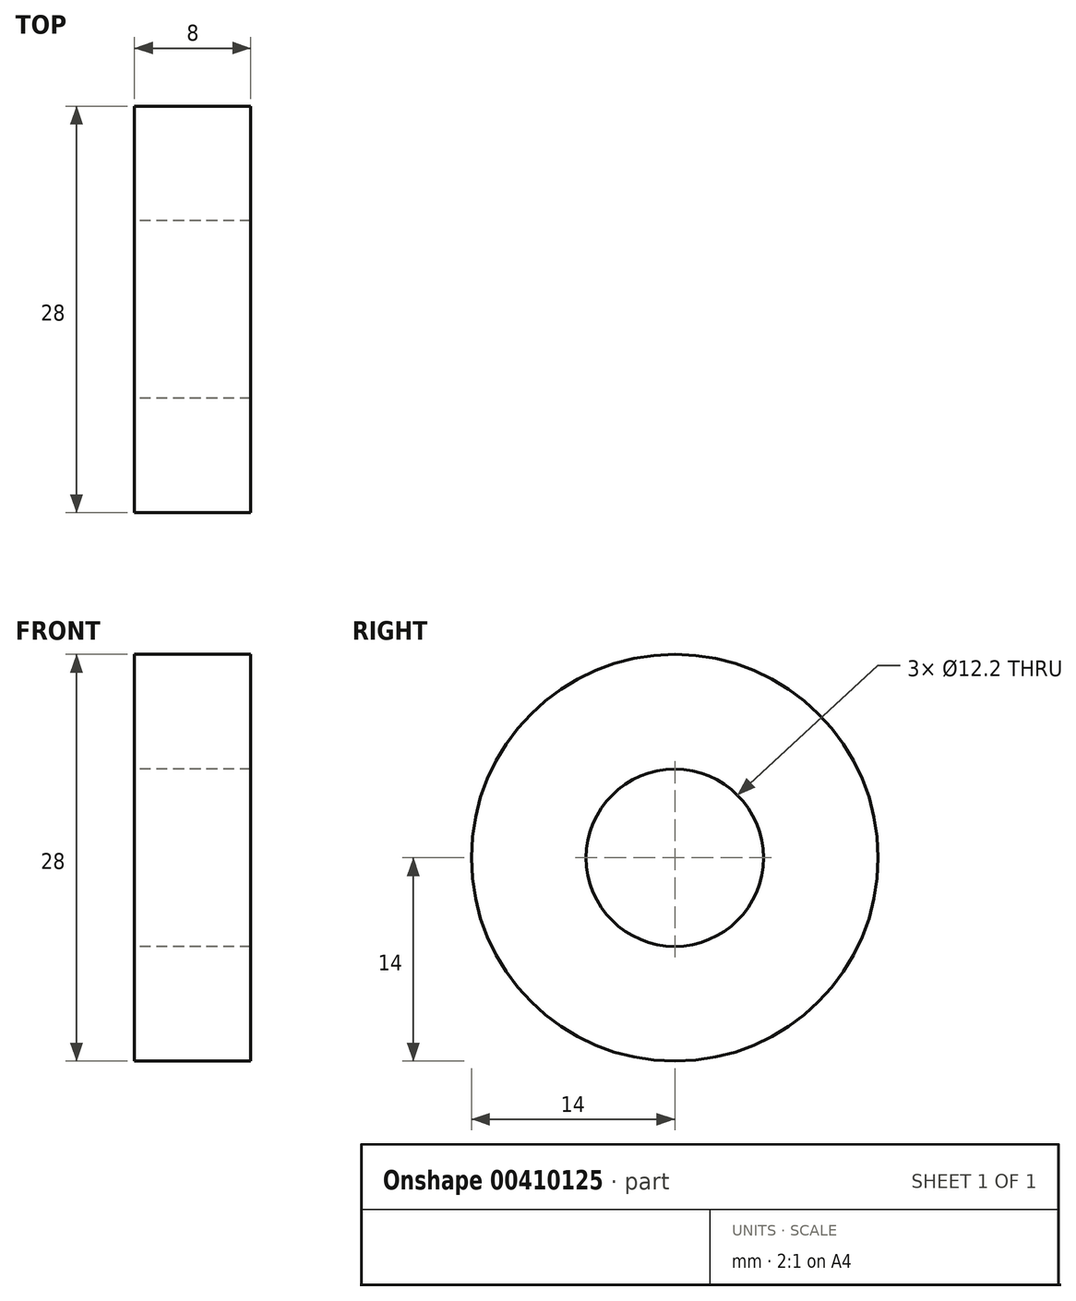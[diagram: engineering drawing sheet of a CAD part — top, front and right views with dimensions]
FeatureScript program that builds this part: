
annotation { "Feature Type Name" : "Feature", "Feature Type Description" : "" }
export const myFeature = defineFeature(function(context is Context, id is Id, definition is map)
    precondition{}
    {
        {
            var Q0;
            Q0=qCreatedBy(makeId("Right.planeOp"),FACE);
            var sketch = newSketch(context, id + "F0", { "sketchPlane" : qUnion([Q0])});
            skCircle(sketch, "E0", {"center": v(0, 0) * mm, "radius": 6.1 * mm});
            skCircle(sketch, "E1", {"center": v(0, 0) * mm, "radius": 14 * mm});
            skSolve(sketch);
        }
        {
            var Q0;
            Q0 = qSketchRegion(id + "F0", true);
            extrude(context, id + "F1", {"entities" : qUnion([Q0]), "depth" : 8 * mm});
        }
    });
